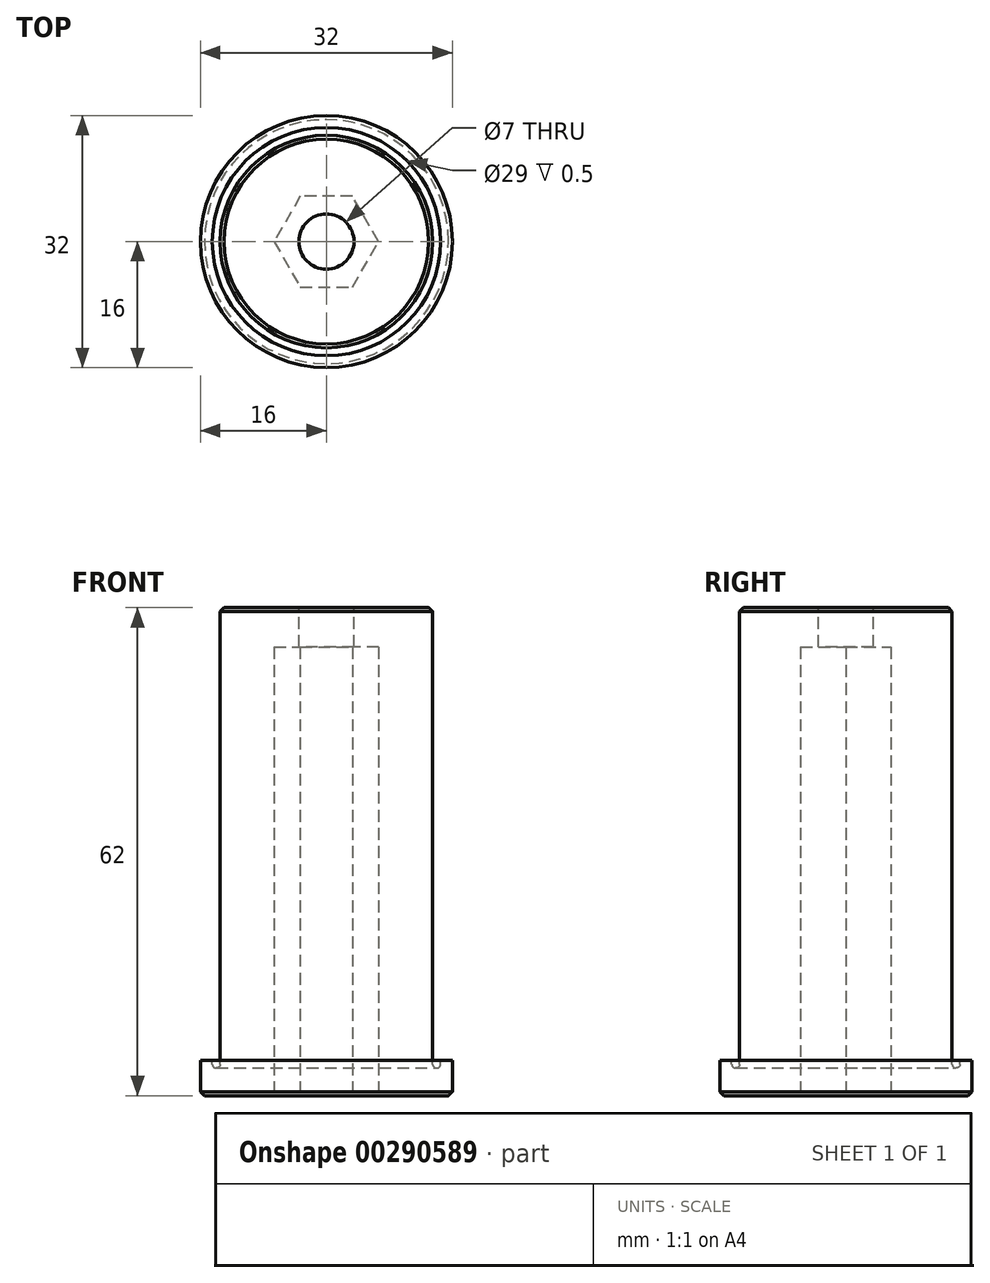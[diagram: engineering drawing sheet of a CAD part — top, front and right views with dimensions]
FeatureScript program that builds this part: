
annotation { "Feature Type Name" : "Feature", "Feature Type Description" : "" }
export const myFeature = defineFeature(function(context is Context, id is Id, definition is map)
    precondition{}
    {
        {
            var Q0;
            Q0=qCreatedBy(makeId("Front.planeOp"),FACE);
            var sketch = newSketch(context, id + "F0", { "sketchPlane" : qUnion([Q0])});
            skLineSegment(sketch, "E0", {"start": v(0, 0) * mm, "end": v(15.5, 0) * mm});
            skLineSegment(sketch, "E1", {"start": v(15.5, 0) * mm, "end": v(16, 0.5) * mm});
            skLineSegment(sketch, "E2", {"start": v(16, 0.5) * mm, "end": v(16, 4.5) * mm});
            skLineSegment(sketch, "E3", {"start": v(16, 4.5) * mm, "end": v(14.5, 4.5) * mm});
            skLineSegment(sketch, "E4", {"start": v(14.5, 4.5) * mm, "end": v(14.5, 4) * mm});
            skLineSegment(sketch, "E5", {"start": v(14, 3.5) * mm, "end": v(14, 3.5) * mm});
            skLineSegment(sketch, "E6", {"start": v(13.5, 4) * mm, "end": v(13.5, 61.5) * mm});
            skLineSegment(sketch, "E7", {"start": v(13.5, 61.5) * mm, "end": v(13, 62) * mm});
            skLineSegment(sketch, "E8", {"start": v(13, 62) * mm, "end": v(3.5, 62) * mm});
            skLineSegment(sketch, "E9", {"start": v(3.5, 62) * mm, "end": v(3.5, 57) * mm});
            skLineSegment(sketch, "E10", {"start": v(3.5, 57) * mm, "end": v(0, 57) * mm});
            skLineSegment(sketch, "E11", {"start": v(0, 57) * mm, "end": v(0, 0) * mm});
            skPoint(sketch, "E12.visualSharp", {"position": v(13.5, 3.5) * mm});
            skArc(sketch, "E12.filletArc", {"start": v(13.5, 4) * mm, "mid": v(13.65, 3.65) * mm, "end": v(14, 3.5) * mm});
            skPoint(sketch, "E13.visualSharp", {"position": v(14.5, 3.5) * mm});
            skArc(sketch, "E13.filletArc", {"start": v(14, 3.5) * mm, "mid": v(14.35, 3.65) * mm, "end": v(14.5, 4) * mm});
            skSolve(sketch);
        }
        {
            var Q0;
            Q0=makeQuery(id+"F0.imprint","IMPRINT",FACE,{"disambiguationData":[TD([[makeQuery(id+"F0.imprint","IMPRINT",EDGE,{"derivedFrom":sQuery(id+"F0.wireOp",EDGE,"E0")}),1.0]])]});
            var Q1;
            Q1=sQuery(id+"F0.wireOp",EDGE,"E11");
            revolve(context, id + "F1", {"entities" : qUnion([Q0]), "axis" : qUnion([Q1]), "revolveType" : RevolveType.FULL});
        }
        {
            var Q0;
            Q0=makeQuery(id+"F1.opRevolve","SWEPT_FACE",FACE,{"disambiguationData":[OSD([sQuery(id+"F0.wireOp",EDGE,"E0")])]});
            var sketch = newSketch(context, id + "F2", { "sketchPlane" : qUnion([Q0])});
            skCircle(sketch, "E14.cCircle", {"center": v(0, 0) * mm, "radius": 5.75 * mm, "construction": true});
            skLineSegment(sketch, "E14.0", {"start": v(6.64, 0) * mm, "end": v(3.32, -5.75) * mm});
            skLineSegment(sketch, "E14.1", {"start": v(3.32, -5.75) * mm, "end": v(-3.32, -5.75) * mm});
            skLineSegment(sketch, "E14.2", {"start": v(-3.32, -5.75) * mm, "end": v(-6.64, 0) * mm});
            skLineSegment(sketch, "E14.3", {"start": v(-6.64, 0) * mm, "end": v(-3.32, 5.75) * mm});
            skLineSegment(sketch, "E14.4", {"start": v(-3.32, 5.75) * mm, "end": v(3.32, 5.75) * mm});
            skLineSegment(sketch, "E14.5", {"start": v(3.32, 5.75) * mm, "end": v(6.64, 0) * mm});
            skPoint(sketch, "E14.0.midPoint", {"position": v(4.98, -2.88) * mm});
            skSolve(sketch);
        }
        {
            var Q0;
            Q0=makeQuery(id+"F2.imprint","IMPRINT",FACE,{"disambiguationData":[TD([[makeQuery(id+"F2.imprint","IMPRINT",EDGE,{"derivedFrom":sQuery(id+"F2.wireOp",EDGE,"E14.0")}),-1.0]])]});
            extrude(context, id + "F3", {"entities" : qUnion([Q0]), "operationType" : NewBodyOperationType.REMOVE, "oppositeDirection" : true, "depth" : 57 * mm});
        }
    });
